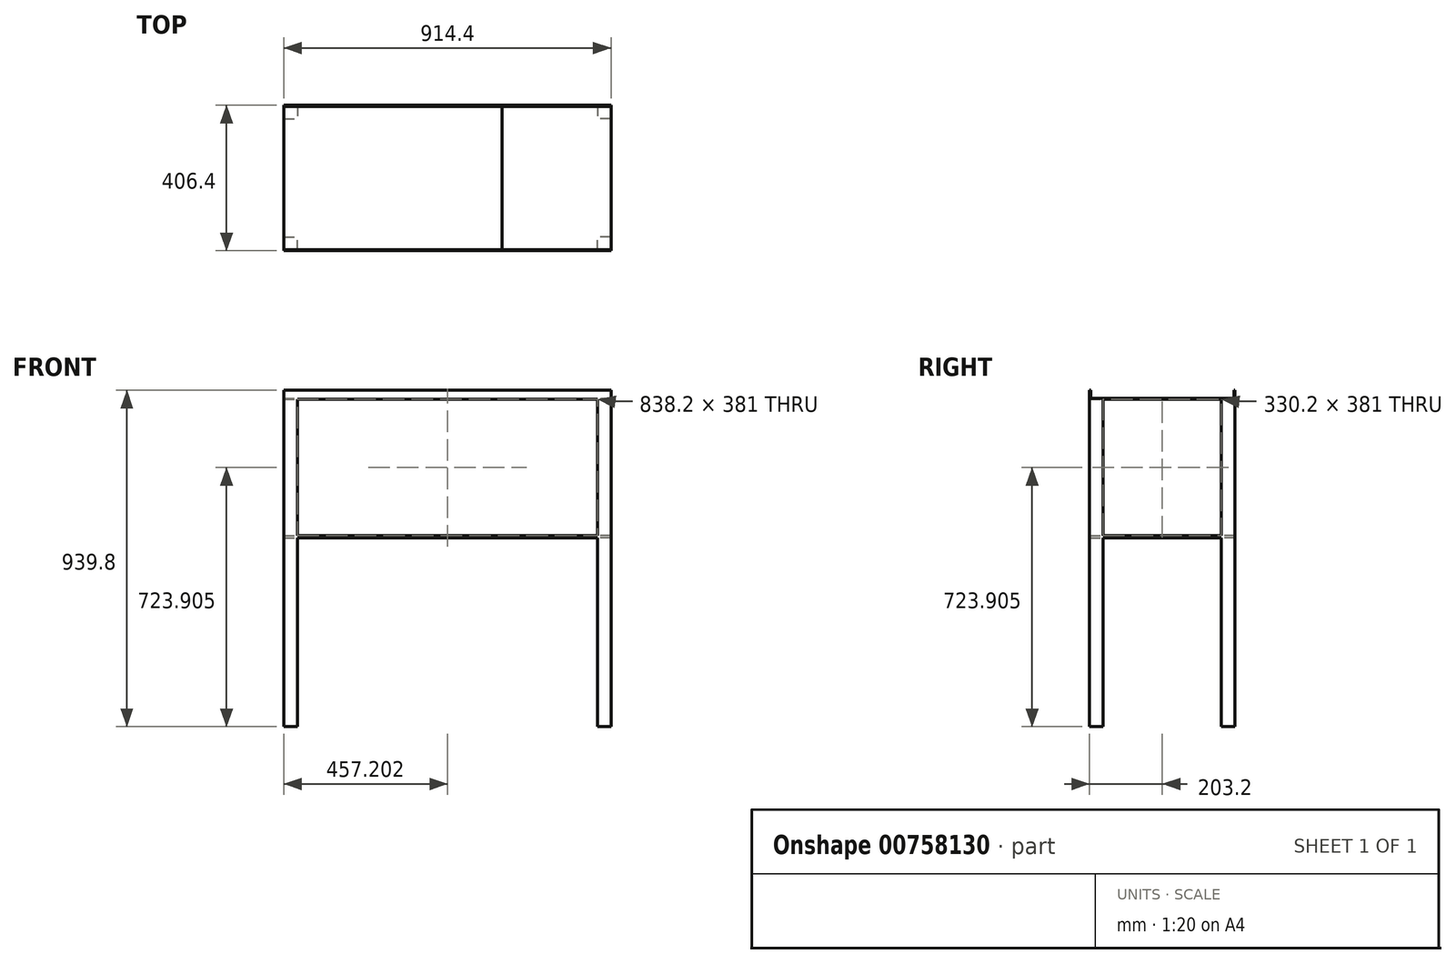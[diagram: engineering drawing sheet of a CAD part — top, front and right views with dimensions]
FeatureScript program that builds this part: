
annotation { "Feature Type Name" : "Feature", "Feature Type Description" : "" }
export const myFeature = defineFeature(function(context is Context, id is Id, definition is map)
    precondition{}
    {
        {
            var Q0;
            Q0=qCreatedBy(makeId("Front.planeOp"),FACE);
            var sketch = newSketch(context, id + "F0", { "sketchPlane" : qUnion([Q0])});
            skLineSegment(sketch, "E0", {"start": v(-451.25, 38.46) * mm, "end": v(-451.25, 13.06) * mm});
            skLineSegment(sketch, "E1", {"start": v(-451.25, 13.06) * mm, "end": v(463.15, 13.06) * mm});
            skLineSegment(sketch, "E2", {"start": v(463.15, 13.06) * mm, "end": v(463.15, 38.46) * mm});
            skLineSegment(sketch, "E3", {"start": v(463.15, 38.46) * mm, "end": v(-451.25, 38.46) * mm});
            skSolve(sketch);
        }
        {
            var Q0;
            Q0 = qSketchRegion(id + "F0", true);
            extrude(context, id + "F1", {"entities" : qUnion([Q0]), "endBound" : BoundingType.SYMMETRIC, "depth" : 406.4 * mm, "offsetDistance" : 25.4 * mm});
        }
        {
            var Q0;
            Q0=makeQuery(id+"F1.opExtrude","SWEPT_FACE",FACE,{"disambiguationData":[OSD([sQuery(id+"F0.wireOp",EDGE,"E3")])]});
            shell(context, id + "F2", {"entities" : qUnion([Q0]), "thickness" : 3.17 * mm});
        }
        {
            var Q0;
            Q0=makeQuery(id+"F1.opExtrude","SWEPT_FACE",FACE,{"disambiguationData":[OSD([sQuery(id+"F0.wireOp",EDGE,"E1")])]});
            var sketch = newSketch(context, id + "F3", { "sketchPlane" : qUnion([Q0])});
            skLineSegment(sketch, "E4.bottom", {"start": v(463.15, 203.2) * mm, "end": v(425.05, 203.2) * mm});
            skLineSegment(sketch, "E4.top", {"start": v(463.15, 165.1) * mm, "end": v(425.05, 165.1) * mm});
            skLineSegment(sketch, "E4.left", {"start": v(463.15, 203.2) * mm, "end": v(463.15, 165.1) * mm});
            skLineSegment(sketch, "E4.right", {"start": v(425.05, 203.2) * mm, "end": v(425.05, 165.1) * mm});
            skLineSegment(sketch, "E5.bottom", {"start": v(463.15, -203.2) * mm, "end": v(425.05, -203.2) * mm});
            skLineSegment(sketch, "E5.top", {"start": v(463.15, -165.1) * mm, "end": v(425.05, -165.1) * mm});
            skLineSegment(sketch, "E5.left", {"start": v(463.15, -203.2) * mm, "end": v(463.15, -165.1) * mm});
            skLineSegment(sketch, "E5.right", {"start": v(425.05, -203.2) * mm, "end": v(425.05, -165.1) * mm});
            skLineSegment(sketch, "E6.bottom", {"start": v(-451.25, 203.2) * mm, "end": v(-413.15, 203.2) * mm});
            skLineSegment(sketch, "E6.top", {"start": v(-451.25, 165.1) * mm, "end": v(-413.15, 165.1) * mm});
            skLineSegment(sketch, "E6.left", {"start": v(-451.25, 203.2) * mm, "end": v(-451.25, 165.1) * mm});
            skLineSegment(sketch, "E6.right", {"start": v(-413.15, 203.2) * mm, "end": v(-413.15, 165.1) * mm});
            skLineSegment(sketch, "E7.bottom", {"start": v(-451.25, -203.2) * mm, "end": v(-413.15, -203.2) * mm});
            skLineSegment(sketch, "E7.top", {"start": v(-451.25, -165.1) * mm, "end": v(-413.15, -165.1) * mm});
            skLineSegment(sketch, "E7.left", {"start": v(-451.25, -203.2) * mm, "end": v(-451.25, -165.1) * mm});
            skLineSegment(sketch, "E7.right", {"start": v(-413.15, -203.2) * mm, "end": v(-413.15, -165.1) * mm});
            skSolve(sketch);
        }
        {
            var Q0;
            Q0 = qSketchRegion(id + "F3", true);
            extrude(context, id + "F4", {"entities" : qUnion([Q0]), "operationType" : NewBodyOperationType.ADD, "depth" : 914.4 * mm, "offsetDistance" : 25.4 * mm});
        }
        {
            var Q0;
            Q0=makeQuery(id+"F4.boolean.opBoolean","MERGE",FACE,{"derivedFrom":[makeQuery(id+"F1.opExtrude","SWEPT_FACE",FACE,{"disambiguationData":[OSD([sQuery(id+"F0.wireOp",EDGE,"E2")])]}),makeQuery(id+"F4.opExtrude","SWEPT_FACE",FACE,{"disambiguationData":[OSD([sQuery(id+"F3.wireOp",EDGE,"E4.left")])]}),makeQuery(id+"F4.opExtrude","SWEPT_FACE",FACE,{"disambiguationData":[OSD([sQuery(id+"F3.wireOp",EDGE,"E5.left")])]})]});
            var sketch = newSketch(context, id + "F5", { "sketchPlane" : qUnion([Q0])});
            skLineSegment(sketch, "E8.bottom", {"start": v(-203.2, -367.94) * mm, "end": v(203.2, -367.94) * mm});
            skLineSegment(sketch, "E8.top", {"start": v(-203.2, -374.29) * mm, "end": v(203.2, -374.29) * mm});
            skLineSegment(sketch, "E8.left", {"start": v(-203.2, -367.94) * mm, "end": v(-203.2, -374.29) * mm});
            skLineSegment(sketch, "E8.right", {"start": v(203.2, -367.94) * mm, "end": v(203.2, -374.29) * mm});
            skSolve(sketch);
        }
        {
            var Q0;
            Q0 = qSketchRegion(id + "F5", true);
            var Q1;
            Q1=makeQuery(id+"F4.boolean.opBoolean","MERGE",FACE,{"derivedFrom":[makeQuery(id+"F1.opExtrude","SWEPT_FACE",FACE,{"disambiguationData":[OSD([sQuery(id+"F0.wireOp",EDGE,"E0")])]}),makeQuery(id+"F4.opExtrude","SWEPT_FACE",FACE,{"disambiguationData":[OSD([sQuery(id+"F3.wireOp",EDGE,"E6.left")])]}),makeQuery(id+"F4.opExtrude","SWEPT_FACE",FACE,{"disambiguationData":[OSD([sQuery(id+"F3.wireOp",EDGE,"E7.left")])]})]});
            extrude(context, id + "F6", {"entities" : qUnion([Q0]), "operationType" : NewBodyOperationType.ADD, "endBound" : BoundingType.UP_TO_SURFACE, "oppositeDirection" : true, "depth" : 25.4 * mm, "endBoundEntityFace" : qUnion([Q1]), "offsetDistance" : 25.4 * mm});
        }
        {
            var Q0;
            Q0=makeQuery(id+"F2.opShell","OFFSET_FACE",FACE,{"disambiguationData":[OSD([sQuery(id+"F0.wireOp",EDGE,"E0")])]});
            extrude(context, id + "F7", {"entities" : qUnion([Q0]), "operationType" : NewBodyOperationType.REMOVE, "oppositeDirection" : true, "depth" : 25.4 * mm, "offsetDistance" : 25.4 * mm});
        }
        {
            var Q0;
            Q0=makeQuery(id+"F2.opShell","OFFSET_FACE",FACE,{"disambiguationData":[OSD([sQuery(id+"F0.wireOp",EDGE,"E2")])]});
            extrude(context, id + "F8", {"entities" : qUnion([Q0]), "operationType" : NewBodyOperationType.REMOVE, "oppositeDirection" : true, "depth" : 25.4 * mm, "offsetDistance" : 25.4 * mm});
        }
        {
            var Q0;
            {var subQ0=sQuery(id+"F0.wireOp",EDGE,"E1");Q0=makeQuery(id+"F8.boolean.opBoolean","MERGE",FACE,{"derivedFrom":[makeQuery(id+"F7.boolean.opBoolean","MERGE",FACE,{"derivedFrom":[makeQuery(id+"F2.opShell","OFFSET_FACE",FACE,{"disambiguationData":[OSD([subQ0])]}),makeQuery(id+"F7.opExtrude","SWEPT_FACE",FACE,{"disambiguationData":[OSD([sQuery(id+"F0.wireOp",EDGE,"E0"),subQ0])]})]}),makeQuery(id+"F8.opExtrude","SWEPT_FACE",FACE,{"disambiguationData":[OSD([subQ0,sQuery(id+"F0.wireOp",EDGE,"E2")])]})]});}
            var sketch = newSketch(context, id + "F9", { "sketchPlane" : qUnion([Q0])});
            skLineSegment(sketch, "E9.bottom", {"start": v(463.15, 200.03) * mm, "end": v(158.35, 200.03) * mm});
            skLineSegment(sketch, "E9.top", {"start": v(463.15, -200.03) * mm, "end": v(158.35, -200.03) * mm});
            skLineSegment(sketch, "E9.left", {"start": v(463.15, 200.03) * mm, "end": v(463.15, -200.03) * mm});
            skLineSegment(sketch, "E9.right", {"start": v(158.35, 200.02) * mm, "end": v(158.35, -200.03) * mm});
            skSolve(sketch);
        }
        {
            var Q0;
            Q0 = qSketchRegion(id + "F9", true);
            extrude(context, id + "F10", {"entities" : qUnion([Q0]), "operationType" : NewBodyOperationType.ADD, "depth" : 0.25 * mm, "offsetDistance" : 25.4 * mm});
        }
    });
